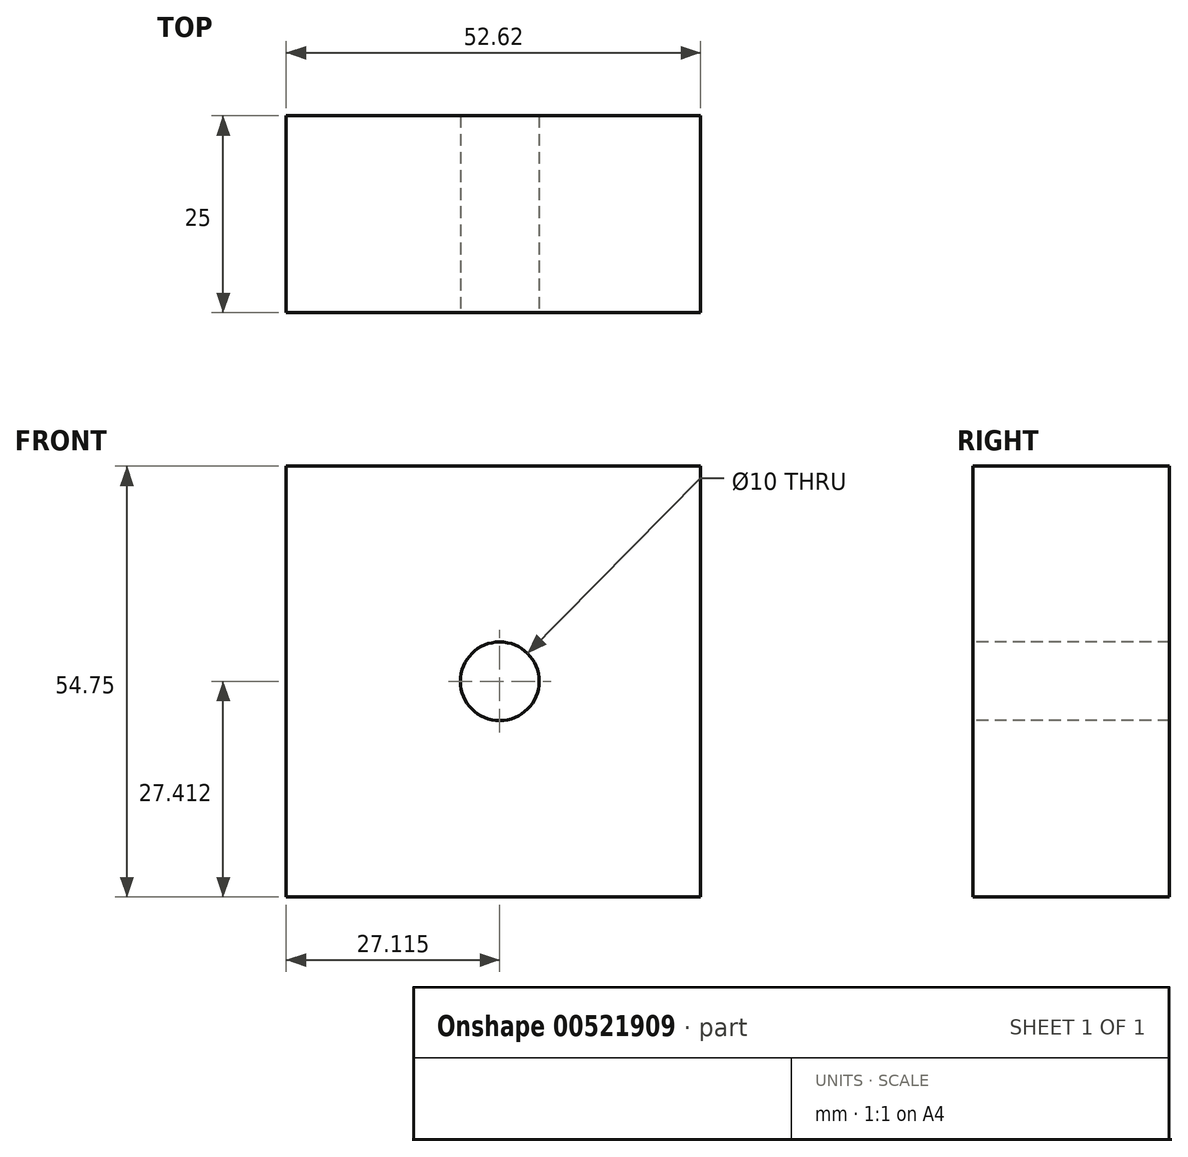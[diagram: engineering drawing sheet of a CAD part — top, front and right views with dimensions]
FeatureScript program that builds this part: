
annotation { "Feature Type Name" : "Feature", "Feature Type Description" : "" }
export const myFeature = defineFeature(function(context is Context, id is Id, definition is map)
    precondition{}
    {
        {
            var Q0;
            Q0=qCreatedBy(makeId("Front.planeOp"),FACE);
            var sketch = newSketch(context, id + "F0", { "sketchPlane" : qUnion([Q0])});
            skLineSegment(sketch, "E0.bottom", {"start": v(-163.15, 39.75) * mm, "end": v(-18.25, 39.75) * mm});
            skLineSegment(sketch, "E0.top", {"start": v(-163.15, -92.6) * mm, "end": v(-18.25, -92.6) * mm});
            skLineSegment(sketch, "E0.left", {"start": v(-163.15, 39.75) * mm, "end": v(-163.15, -92.6) * mm});
            skLineSegment(sketch, "E0.right", {"start": v(-18.25, 39.75) * mm, "end": v(-18.25, -92.6) * mm});
            skSolve(sketch);
        }
        {
            var Q0;
            Q0 = qSketchRegion(id + "F0", true);
            extrude(context, id + "F1", {"entities" : qUnion([Q0]), "depth" : 25 * mm, "offsetDistance" : 25 * mm});
        }
        {
            var Q0;
            Q0=makeQuery(id+"F1.opExtrude","SWEPT_BODY",BODY,{"disambiguationData":[OSD([sQuery(id+"F0.wireOp",EDGE,"E0.bottom"),sQuery(id+"F0.wireOp",EDGE,"E0.top"),sQuery(id+"F0.wireOp",EDGE,"E0.left"),sQuery(id+"F0.wireOp",EDGE,"E0.right")])]});
            deleteBodies(context, id + "F2", {"entities" : qUnion([Q0])});
        }
        {
            var Q0;
            Q0=qCreatedBy(makeId("Front.planeOp"),FACE);
            var sketch = newSketch(context, id + "F3", { "sketchPlane" : qUnion([Q0])});
            skLineSegment(sketch, "E1.bottom", {"start": v(-76.27, 37.7) * mm, "end": v(-23.65, 37.7) * mm});
            skLineSegment(sketch, "E1.top", {"start": v(-76.27, -17.05) * mm, "end": v(-23.65, -17.05) * mm});
            skLineSegment(sketch, "E1.left", {"start": v(-76.27, 37.7) * mm, "end": v(-76.27, -17.05) * mm});
            skLineSegment(sketch, "E1.right", {"start": v(-23.65, 37.7) * mm, "end": v(-23.65, -17.05) * mm});
            skSolve(sketch);
        }
        {
            var Q0;
            Q0 = qSketchRegion(id + "F3", true);
            extrude(context, id + "F4", {"entities" : qUnion([Q0]), "depth" : 25 * mm, "offsetDistance" : 25 * mm});
        }
        {
            var Q0;
            Q0=makeQuery(id+"F4.opExtrude","CAP_FACE",FACE,{"disambiguationData":[OSD([sQuery(id+"F3.wireOp",EDGE,"E1.bottom"),sQuery(id+"F3.wireOp",EDGE,"E1.top"),sQuery(id+"F3.wireOp",EDGE,"E1.left"),sQuery(id+"F3.wireOp",EDGE,"E1.right")])],"isStart":false});
            var sketch = newSketch(context, id + "F5", { "sketchPlane" : qUnion([Q0])});
            skPoint(sketch, "E2", {"position": v(-49.15, 10.36) * mm});
            skSolve(sketch);
        }
        {
            var Q0;
            Q0=sQuery(id+"F5.wireOp",VERTEX,"E2");
            var Q1;
            Q1=makeQuery(id+"F4.opExtrude","SWEPT_BODY",BODY,{"disambiguationData":[OSD([sQuery(id+"F3.wireOp",EDGE,"E1.bottom"),sQuery(id+"F3.wireOp",EDGE,"E1.top"),sQuery(id+"F3.wireOp",EDGE,"E1.left"),sQuery(id+"F3.wireOp",EDGE,"E1.right")])]});
            hole(context, id + "F6", {"style" : HoleStyle.C_BORE, "endStyle" : HoleEndStyle.BLIND, "holeDiameter" : 10 * mm, "cBoreDiameter" : 10 * mm, "cBoreDepth" : 5 * mm, "holeDepth" : 50 * mm, "isTappedThrough" : true, "tappedDepth" : 12 * mm, "tapClearance" : 3, "startFromSketch" : true, "locations" : qUnion([Q0]), "scope" : qUnion([Q1])});
        }
    });
